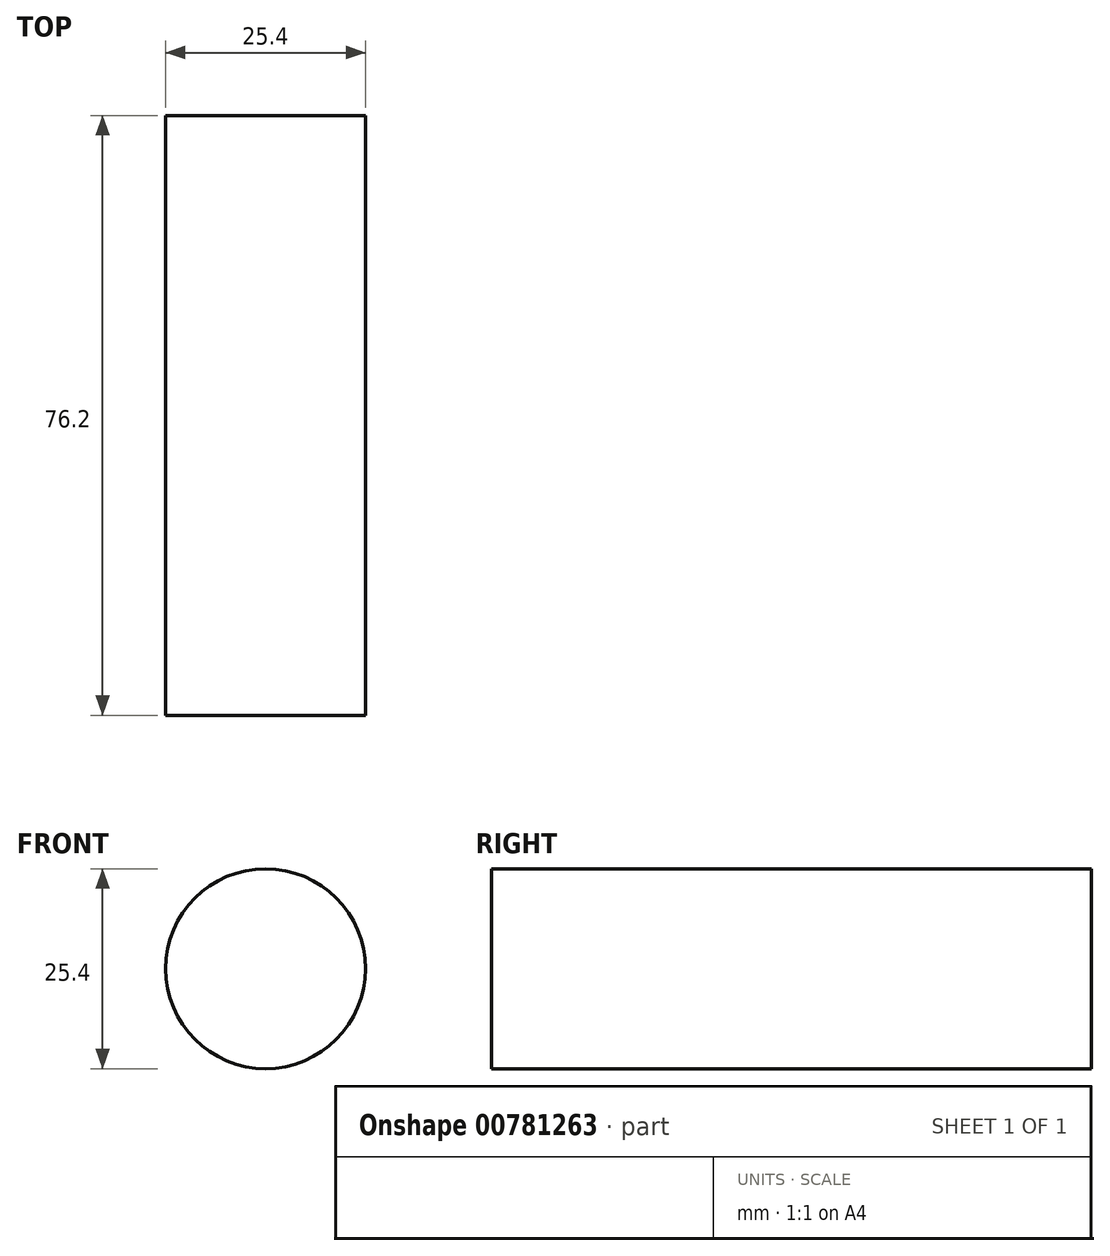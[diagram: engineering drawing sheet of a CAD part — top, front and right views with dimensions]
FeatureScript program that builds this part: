
annotation { "Feature Type Name" : "Feature", "Feature Type Description" : "" }
export const myFeature = defineFeature(function(context is Context, id is Id, definition is map)
    precondition{}
    {
        {
            var Q0;
            Q0=qCreatedBy(makeId("Front.planeOp"),FACE);
            var sketch = newSketch(context, id + "F0", { "sketchPlane" : qUnion([Q0])});
            skCircle(sketch, "E0", {"center": v(0, 0) * mm, "radius": 12.7 * mm});
            skSolve(sketch);
        }
        {
            var Q0;
            Q0=qSketchRegion(id+"F0",true);
            extrude(context, id + "F1", {"entities" : qUnion([Q0]), "depth" : 76.2 * mm, "offsetDistance" : 25.4 * mm});
        }
    });
